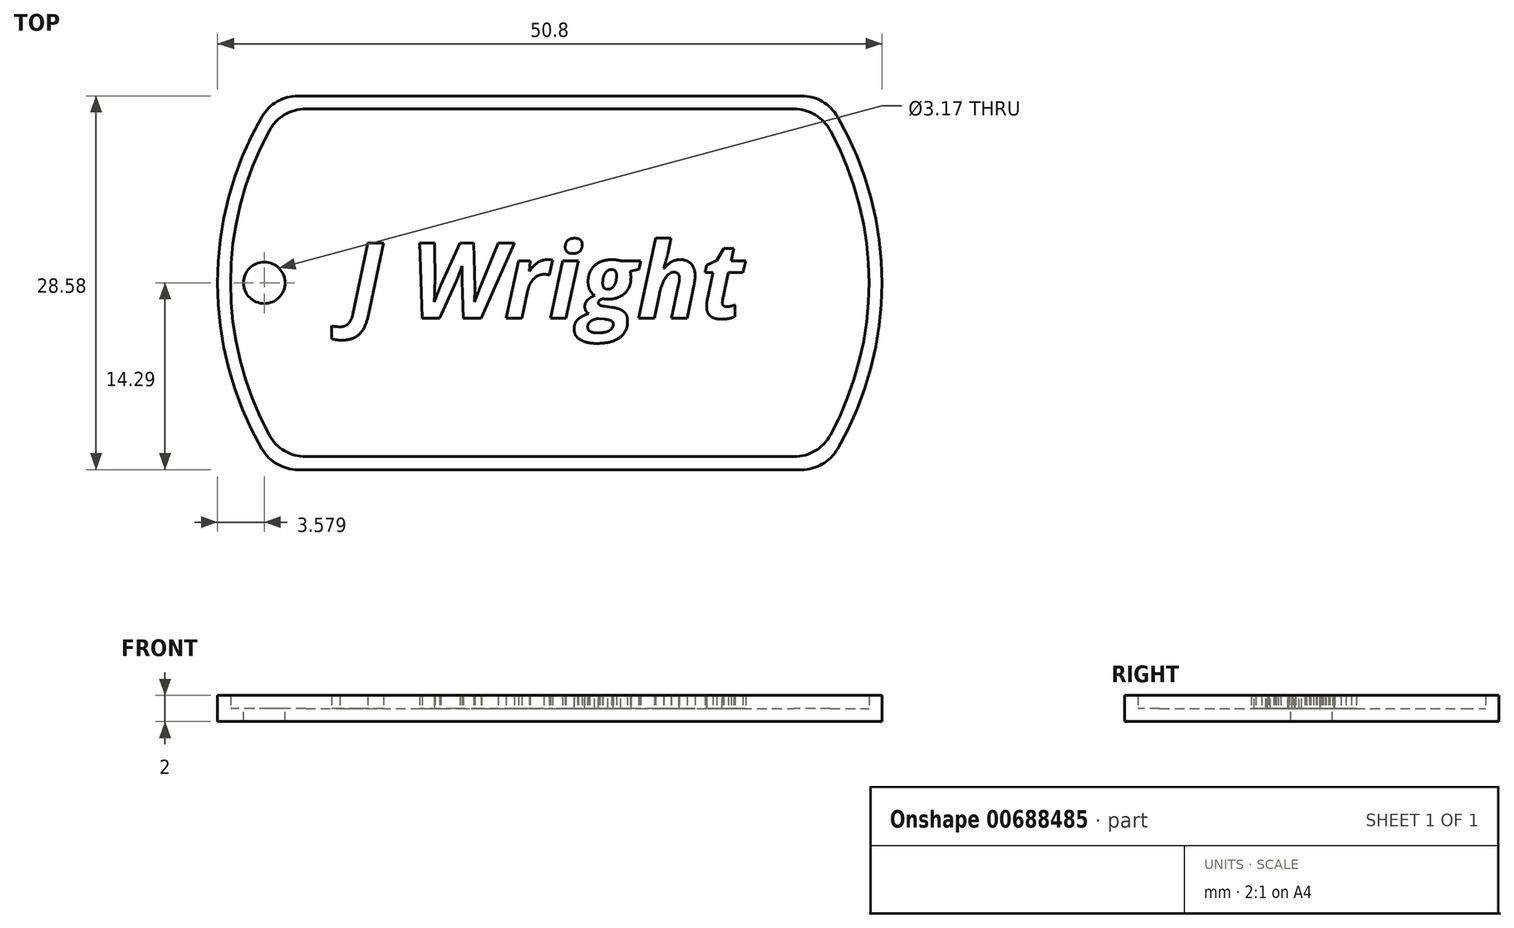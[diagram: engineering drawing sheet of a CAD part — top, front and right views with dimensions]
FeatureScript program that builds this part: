
annotation { "Feature Type Name" : "Feature", "Feature Type Description" : "" }
export const myFeature = defineFeature(function(context is Context, id is Id, definition is map)
    precondition{}
    {
        {
            var Q0;
            Q0=qCreatedBy(makeId("Top.planeOp"),FACE);
            var sketch = newSketch(context, id + "F0", { "sketchPlane" : qUnion([Q0])});
            skArc(sketch, "E0", {"start": v(-22, 12.7) * mm, "mid": v(-25.4, 0) * mm, "end": v(-22, -12.7) * mm});
            skLineSegment(sketch, "E1.top", {"start": v(-19.25, -14.29) * mm, "end": v(19.25, -14.29) * mm});
            skArc(sketch, "E2.trimOffspring", {"start": v(22, -12.7) * mm, "mid": v(25.4, 0) * mm, "end": v(22, 12.7) * mm});
            skLineSegment(sketch, "E3", {"start": v(-19.25, 14.29) * mm, "end": v(19.25, 14.29) * mm});
            skPoint(sketch, "E4.visualSharp", {"position": v(-21, 14.29) * mm});
            skArc(sketch, "E4.filletArc", {"start": v(-19.25, 14.29) * mm, "mid": v(-20.83, 13.86) * mm, "end": v(-22, 12.7) * mm});
            skPoint(sketch, "E5.visualSharp", {"position": v(21, 14.29) * mm});
            skArc(sketch, "E5.filletArc", {"start": v(22, 12.7) * mm, "mid": v(20.83, 13.86) * mm, "end": v(19.25, 14.29) * mm});
            skPoint(sketch, "E6.visualSharp", {"position": v(21, -14.29) * mm});
            skArc(sketch, "E6.filletArc", {"start": v(19.25, -14.29) * mm, "mid": v(20.83, -13.86) * mm, "end": v(22, -12.7) * mm});
            skPoint(sketch, "E7.visualSharp", {"position": v(-21, -14.29) * mm});
            skArc(sketch, "E7.filletArc", {"start": v(-22, -12.7) * mm, "mid": v(-20.83, -13.86) * mm, "end": v(-19.25, -14.29) * mm});
            skSolve(sketch);
        }
        {
            var Q0;
            Q0=makeQuery(id+"F0.imprint","IMPRINT",FACE,{"disambiguationData":[TD([[makeQuery(id+"F0.imprint","IMPRINT",EDGE,{"derivedFrom":sQuery(id+"F0.wireOp",EDGE,"E0")}),1.0]])]});
            extrude(context, id + "F1", {"entities" : qUnion([Q0]), "depth" : 1 * mm, "offsetDistance" : 25.4 * mm});
        }
        {
            var Q0;
            Q0=makeQuery(id+"F1.opExtrude","CAP_FACE",FACE,{"disambiguationData":[OSD([sQuery(id+"F0.wireOp",EDGE,"E0"),sQuery(id+"F0.wireOp",EDGE,"E1.top"),sQuery(id+"F0.wireOp",EDGE,"E2.trimOffspring"),sQuery(id+"F0.wireOp",EDGE,"E3"),sQuery(id+"F0.wireOp",EDGE,"E4.filletArc"),sQuery(id+"F0.wireOp",EDGE,"E5.filletArc"),sQuery(id+"F0.wireOp",EDGE,"E6.filletArc"),sQuery(id+"F0.wireOp",EDGE,"E7.filletArc")])],"isStart":false});
            var sketch = newSketch(context, id + "F2", { "sketchPlane" : qUnion([Q0])});
            skLineSegment(sketch, "E8.0", {"start": v(-18.66, 13.29) * mm, "end": v(18.66, 13.29) * mm});
            skArc(sketch, "E8.1", {"start": v(-21.45, 11.63) * mm, "mid": v(-24.4, 0) * mm, "end": v(-21.45, -11.63) * mm});
            skLineSegment(sketch, "E8.2", {"start": v(-18.66, -13.29) * mm, "end": v(18.66, -13.29) * mm});
            skArc(sketch, "E8.3", {"start": v(21.45, -11.63) * mm, "mid": v(24.4, 0) * mm, "end": v(21.45, 11.63) * mm});
            skPoint(sketch, "E9.visualSharp", {"position": v(-20.46, 13.29) * mm});
            skArc(sketch, "E9.filletArc", {"start": v(-18.66, 13.29) * mm, "mid": v(-20.29, 12.84) * mm, "end": v(-21.45, 11.63) * mm});
            skPoint(sketch, "E10.visualSharp", {"position": v(20.46, 13.29) * mm});
            skArc(sketch, "E10.filletArc", {"start": v(21.45, 11.63) * mm, "mid": v(20.29, 12.84) * mm, "end": v(18.66, 13.29) * mm});
            skPoint(sketch, "E11.visualSharp", {"position": v(20.46, -13.29) * mm});
            skArc(sketch, "E11.filletArc", {"start": v(18.66, -13.29) * mm, "mid": v(20.29, -12.84) * mm, "end": v(21.45, -11.63) * mm});
            skPoint(sketch, "E12.visualSharp", {"position": v(-20.46, -13.29) * mm});
            skArc(sketch, "E12.filletArc", {"start": v(-21.45, -11.63) * mm, "mid": v(-20.29, -12.84) * mm, "end": v(-18.66, -13.29) * mm});
            skLineSegment(sketch, "E13.0", {"start": v(-19.25, 14.29) * mm, "end": v(19.25, 14.29) * mm});
            skArc(sketch, "E13.1", {"start": v(-22, 12.7) * mm, "mid": v(-25.4, 0) * mm, "end": v(-22, -12.7) * mm});
            skLineSegment(sketch, "E13.2", {"start": v(-19.25, -14.29) * mm, "end": v(19.25, -14.29) * mm});
            skArc(sketch, "E13.3", {"start": v(22, -12.7) * mm, "mid": v(25.4, 0) * mm, "end": v(22, 12.7) * mm});
            skPoint(sketch, "E14.visualSharp", {"position": v(-21, -14.29) * mm});
            skArc(sketch, "E14.filletArc", {"start": v(-22, -12.7) * mm, "mid": v(-20.83, -13.86) * mm, "end": v(-19.25, -14.29) * mm});
            skPoint(sketch, "E15.visualSharp", {"position": v(21, -14.29) * mm});
            skArc(sketch, "E15.filletArc", {"start": v(19.25, -14.29) * mm, "mid": v(20.83, -13.86) * mm, "end": v(22, -12.7) * mm});
            skPoint(sketch, "E16.visualSharp", {"position": v(21, 14.29) * mm});
            skArc(sketch, "E16.filletArc", {"start": v(22, 12.7) * mm, "mid": v(20.83, 13.86) * mm, "end": v(19.25, 14.29) * mm});
            skPoint(sketch, "E17.visualSharp", {"position": v(-21, 14.29) * mm});
            skArc(sketch, "E17.filletArc", {"start": v(-19.25, 14.29) * mm, "mid": v(-20.83, 13.86) * mm, "end": v(-22, 12.7) * mm});
            skSolve(sketch);
        }
        {
            var Q0;
            Q0=makeQuery(id+"F2.imprint","IMPRINT",FACE,{"disambiguationData":[TD([[makeQuery(id+"F2.imprint","IMPRINT",EDGE,{"derivedFrom":sQuery(id+"F2.wireOp",EDGE,"E8.0")}),1.0]])]});
            extrude(context, id + "F3", {"entities" : qUnion([Q0]), "operationType" : NewBodyOperationType.ADD, "depth" : 1 * mm, "offsetDistance" : 25.4 * mm});
        }
        {
            var Q0;
            Q0=makeQuery(id+"F1.opExtrude","CAP_FACE",FACE,{"disambiguationData":[OSD([sQuery(id+"F0.wireOp",EDGE,"E0"),sQuery(id+"F0.wireOp",EDGE,"E1.top"),sQuery(id+"F0.wireOp",EDGE,"E2.trimOffspring"),sQuery(id+"F0.wireOp",EDGE,"E3"),sQuery(id+"F0.wireOp",EDGE,"E4.filletArc"),sQuery(id+"F0.wireOp",EDGE,"E5.filletArc"),sQuery(id+"F0.wireOp",EDGE,"E6.filletArc"),sQuery(id+"F0.wireOp",EDGE,"E7.filletArc")])],"isStart":false});
            var sketch = newSketch(context, id + "F4", { "sketchPlane" : qUnion([Q0])});
            skCircle(sketch, "E18", {"center": v(-21.82, 0) * mm, "radius": 1.59 * mm});
            skSolve(sketch);
        }
        {
            var Q0;
            Q0=makeQuery(id+"F4.imprint","IMPRINT",FACE,{"disambiguationData":[TD([[makeQuery(id+"F4.imprint","IMPRINT",EDGE,{"derivedFrom":sQuery(id+"F4.wireOp",EDGE,"E18")}),1.0]])]});
            extrude(context, id + "F5", {"entities" : qUnion([Q0]), "operationType" : NewBodyOperationType.REMOVE, "oppositeDirection" : true, "depth" : 1 * mm, "offsetDistance" : 25.4 * mm});
        }
        {
            var Q0;
            Q0=makeQuery(id+"F2.imprint","IMPRINT",FACE,{"disambiguationData":[TD([[makeQuery(id+"F2.imprint","IMPRINT",EDGE,{"derivedFrom":sQuery(id+"F2.wireOp",EDGE,"E8.0")}),-1.0]])]});
            var sketch = newSketch(context, id + "F6", { "sketchPlane" : qUnion([Q0])});
            skText(sketch, "E19", { "text": "J Wright", "fontName": "OpenSans-BoldItalic.ttf"});
            const initialGuessF6  = {"E19": [-0.01541, -0.0027, 1, 0, 0.00579]};
            skSetInitialGuess(sketch, initialGuessF6);
            skSolve(sketch);
        }
        {
            var Q0;
            Q0 = qSketchRegion(id + "F6", true);
            extrude(context, id + "F7", {"entities" : qUnion([Q0]), "operationType" : NewBodyOperationType.ADD, "depth" : 1 * mm, "offsetDistance" : 25.4 * mm});
        }
    });
